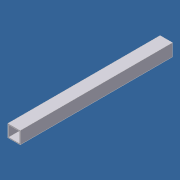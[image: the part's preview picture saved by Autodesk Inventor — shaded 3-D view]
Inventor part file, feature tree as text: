
AUTODESK INVENTOR PART (.ipt)
format: ipt  version: 2012 (Build 160160000, 160)  size: 70,656 bytes
history: native  units: in
note: dims shown in document units (in); Inventor stores cm internally (conversion verified against a paired STEP export)
features: extrude x1, sketch x1
ambient origin geometry x8: Origin, YZ Plane, XZ Plane, XY Plane, X Axis, Y Axis, Z Axis, Center Point
bodies: Solid1 (feature_tree)
feature tree (2):
  extrude  "Extrusion1"  Depth=1.75in
  sketch  "Sketch1"  dims[d0=0.125in d1=1.75in d2=21.5in d3=0.0in]
